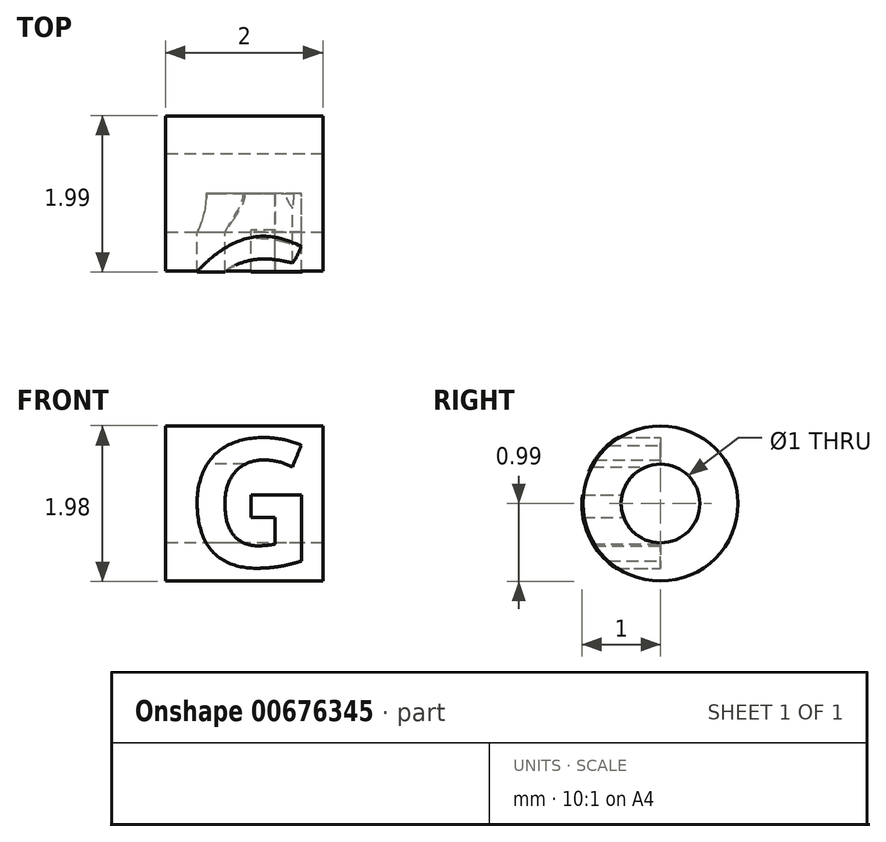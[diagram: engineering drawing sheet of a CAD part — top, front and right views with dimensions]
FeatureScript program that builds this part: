
annotation { "Feature Type Name" : "Feature", "Feature Type Description" : "" }
export const myFeature = defineFeature(function(context is Context, id is Id, definition is map)
    precondition{}
    {
        {
            var Q0;
            Q0=qCreatedBy(makeId("Right.planeOp"),FACE);
            var sketch = newSketch(context, id + "F0", { "sketchPlane" : qUnion([Q0])});
            skCircle(sketch, "E0", {"center": v(0, 0) * mm, "radius": 0.5 * mm});
            skCircle(sketch, "E1", {"center": v(0, 0) * mm, "radius": 1 * mm});
            skCircle(sketch, "E2", {"center": v(0, 0) * mm, "radius": 0.98 * mm});
            skSolve(sketch);
        }
        {
            var Q0;
            Q0=makeQuery(id+"F0.imprint","IMPRINT",FACE,{"disambiguationData":[TD([[makeQuery(id+"F0.imprint","IMPRINT",EDGE,{"derivedFrom":sQuery(id+"F0.wireOp",EDGE,"E0")}),-1.0]])]});
            var Q1;
            Q1=makeQuery(id+"F0.imprint","IMPRINT",FACE,{"disambiguationData":[TD([[makeQuery(id+"F0.imprint","IMPRINT",EDGE,{"derivedFrom":sQuery(id+"F0.wireOp",EDGE,"E1")}),1.0]])]});
            extrude(context, id + "F1", {"entities" : qUnion([Q0, Q1]), "depth" : 2 * mm, "offsetDistance" : 25 * mm});
        }
        {
            var Q0;
            Q0=qCreatedBy(makeId("Front.planeOp"),FACE);
            var sketch = newSketch(context, id + "F2", { "sketchPlane" : qUnion([Q0])});
            skText(sketch, "E3", { "text": "G", "fontName": "OpenSans-Bold.ttf"});
            const initialGuessF2  = {"E3": [0.00027, -0.0008, 1, 0, 0.00163]};
            skSetInitialGuess(sketch, initialGuessF2);
            skSolve(sketch);
        }
        {
            var Q0;
            Q0=qSketchRegion(id+"F2",true);
            var Q1;
            Q1=qConstructionFilter(qBodyType(qCreatedBy(id+"F2",EDGE),BodyType.WIRE),ConstructionObject.NO);
            var Q2;
            Q2=makeQuery(id+"F1.opExtrude","SWEPT_FACE",FACE,{"disambiguationData":[OSD([sQuery(id+"F0.wireOp",EDGE,"E1")])]});
            var Q3;
            Q3=makeQuery(id+"F1.opExtrude","SWEPT_BODY",BODY,{"disambiguationData":[OSD([sQuery(id+"F0.wireOp",EDGE,"E0"),sQuery(id+"F0.wireOp",EDGE,"E1")])]});
            var Q4;
            Q4=sQuery(id+"F0.wireOp",VERTEX,"27635d6e-dcd6-4653-b727-4819003c0945");
            extrude(context, id + "F3", {"entities" : qUnion([Q0]), "operationType" : NewBodyOperationType.INTERSECT, "surfaceEntities" : qUnion([Q1]), "endBound" : BoundingType.UP_TO_SURFACE, "endBoundEntityFace" : qUnion([Q2]), "endBoundEntityBody" : qUnion([Q3]), "endBoundEntityVertex" : qUnion([Q4]), "depth" : 25 * mm, "offsetDistance" : 25 * mm});
        }
        {
            var Q0;
            Q0=makeQuery(id+"F0.imprint","IMPRINT",FACE,{"disambiguationData":[TD([[makeQuery(id+"F0.imprint","IMPRINT",EDGE,{"derivedFrom":sQuery(id+"F0.wireOp",EDGE,"E0")}),-1.0]])]});
            extrude(context, id + "F4", {"entities" : qUnion([Q0]), "depth" : 2 * mm, "offsetDistance" : 25 * mm});
        }
    });
